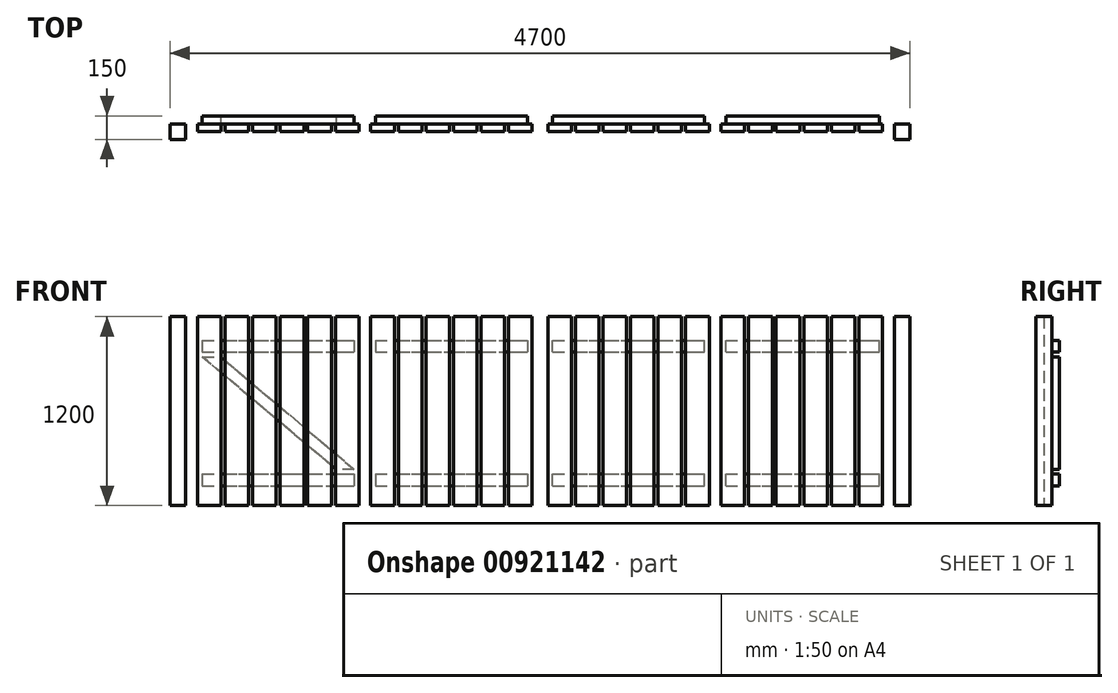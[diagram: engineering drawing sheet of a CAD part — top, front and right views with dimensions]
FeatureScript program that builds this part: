
annotation { "Feature Type Name" : "Feature", "Feature Type Description" : "" }
export const myFeature = defineFeature(function(context is Context, id is Id, definition is map)
    precondition{}
    {
        {
            var Q0;
            Q0=qCreatedBy(makeId("Front.planeOp"),FACE);
            var sketch = newSketch(context, id + "F0", { "sketchPlane" : qUnion([Q0])});
            skLineSegment(sketch, "E0.bottom", {"start": v(-2350, 1200) * mm, "end": v(-2250, 1200) * mm});
            skLineSegment(sketch, "E0.top", {"start": v(-2350, 0) * mm, "end": v(-2250, 0) * mm});
            skLineSegment(sketch, "E0.left", {"start": v(-2350, 1200) * mm, "end": v(-2350, 0) * mm});
            skLineSegment(sketch, "E0.right", {"start": v(-2250, 1200) * mm, "end": v(-2250, 0) * mm});
            skLineSegment(sketch, "E1.bottom", {"start": v(2250, 0) * mm, "end": v(2350, 0) * mm});
            skLineSegment(sketch, "E1.top", {"start": v(2250, 1200) * mm, "end": v(2350, 1200) * mm});
            skLineSegment(sketch, "E1.left", {"start": v(2250, 0) * mm, "end": v(2250, 1200) * mm});
            skLineSegment(sketch, "E1.right", {"start": v(2350, 0) * mm, "end": v(2350, 1200) * mm});
            skSolve(sketch);
        }
        {
            var Q0;
            Q0=makeQuery(id+"F0.imprint","IMPRINT",FACE,{"disambiguationData":[TD([[makeQuery(id+"F0.imprint","IMPRINT",EDGE,{"derivedFrom":sQuery(id+"F0.wireOp",EDGE,"E0.bottom")}),-1.0]])]});
            var Q1;
            Q1=makeQuery(id+"F0.imprint","IMPRINT",FACE,{"disambiguationData":[TD([[makeQuery(id+"F0.imprint","IMPRINT",EDGE,{"derivedFrom":sQuery(id+"F0.wireOp",EDGE,"E1.bottom")}),1.0]])]});
            extrude(context, id + "F1", {"entities" : qUnion([Q0, Q1]), "depth" : 100 * mm, "offsetDistance" : 25.4 * mm});
        }
        {
            var Q0;
            Q0=qCreatedBy(makeId("Front.planeOp"),FACE);
            var sketch = newSketch(context, id + "F2", { "sketchPlane" : qUnion([Q0])});
            skLineSegment(sketch, "E2.bottom", {"start": v(-2175, 1200) * mm, "end": v(-2025, 1200) * mm});
            skLineSegment(sketch, "E2.top", {"start": v(-2175, 0) * mm, "end": v(-2025, 0) * mm});
            skLineSegment(sketch, "E2.left", {"start": v(-2175, 1200) * mm, "end": v(-2175, 0) * mm});
            skLineSegment(sketch, "E2.right", {"start": v(-2025, 1200) * mm, "end": v(-2025, 0) * mm});
            skLineSegment(sketch, "E3.bottom", {"start": v(-50, 0) * mm, "end": v(-200, 0) * mm});
            skLineSegment(sketch, "E3.top", {"start": v(-50, 1200) * mm, "end": v(-200, 1200) * mm});
            skLineSegment(sketch, "E3.left", {"start": v(-50, 0) * mm, "end": v(-50, 1200) * mm});
            skLineSegment(sketch, "E3.right", {"start": v(-200, 0) * mm, "end": v(-200, 1200) * mm});
            skLineSegment(sketch, "E4.bottom", {"start": v(50, 0) * mm, "end": v(200, 0) * mm});
            skLineSegment(sketch, "E4.top", {"start": v(50, 1200) * mm, "end": v(200, 1200) * mm});
            skLineSegment(sketch, "E4.left", {"start": v(50, 0) * mm, "end": v(50, 1200) * mm});
            skLineSegment(sketch, "E4.right", {"start": v(200, 0) * mm, "end": v(200, 1200) * mm});
            skLineSegment(sketch, "E5.bottom", {"start": v(2175, 0) * mm, "end": v(2025, 0) * mm});
            skLineSegment(sketch, "E5.top", {"start": v(2175, 1200) * mm, "end": v(2025, 1200) * mm});
            skLineSegment(sketch, "E5.left", {"start": v(2175, 0) * mm, "end": v(2175, 1200) * mm});
            skLineSegment(sketch, "E5.right", {"start": v(2025, 0) * mm, "end": v(2025, 1200) * mm});
            skLineSegment(sketch, "E6.1.0.0", {"start": v(-2000, 1200) * mm, "end": v(-1850, 1200) * mm});
            skLineSegment(sketch, "E6.1.0.1", {"start": v(-2000, 1200) * mm, "end": v(-2000, 0) * mm});
            skLineSegment(sketch, "E6.1.0.2", {"start": v(-2000, 0) * mm, "end": v(-1850, 0) * mm});
            skLineSegment(sketch, "E6.1.0.3", {"start": v(-1850, 1200) * mm, "end": v(-1850, 0) * mm});
            skLineSegment(sketch, "E6.2.0.0", {"start": v(-1825, 1200) * mm, "end": v(-1675, 1200) * mm});
            skLineSegment(sketch, "E6.2.0.1", {"start": v(-1825, 1200) * mm, "end": v(-1825, 0) * mm});
            skLineSegment(sketch, "E6.2.0.2", {"start": v(-1825, 0) * mm, "end": v(-1675, 0) * mm});
            skLineSegment(sketch, "E6.2.0.3", {"start": v(-1675, 1200) * mm, "end": v(-1675, 0) * mm});
            skLineSegment(sketch, "E6.3.0.0", {"start": v(-1650, 1200) * mm, "end": v(-1500, 1200) * mm});
            skLineSegment(sketch, "E6.3.0.1", {"start": v(-1650, 1200) * mm, "end": v(-1650, 0) * mm});
            skLineSegment(sketch, "E6.3.0.2", {"start": v(-1650, 0) * mm, "end": v(-1500, 0) * mm});
            skLineSegment(sketch, "E6.3.0.3", {"start": v(-1500, 1200) * mm, "end": v(-1500, 0) * mm});
            skLineSegment(sketch, "E6.4.0.0", {"start": v(-1475, 1200) * mm, "end": v(-1325, 1200) * mm});
            skLineSegment(sketch, "E6.4.0.1", {"start": v(-1475, 1200) * mm, "end": v(-1475, 0) * mm});
            skLineSegment(sketch, "E6.4.0.2", {"start": v(-1475, 0) * mm, "end": v(-1325, 0) * mm});
            skLineSegment(sketch, "E6.4.0.3", {"start": v(-1325, 1200) * mm, "end": v(-1325, 0) * mm});
            skLineSegment(sketch, "E6.5.0.0", {"start": v(-1300, 1200) * mm, "end": v(-1150, 1200) * mm});
            skLineSegment(sketch, "E6.5.0.1", {"start": v(-1300, 1200) * mm, "end": v(-1300, 0) * mm});
            skLineSegment(sketch, "E6.5.0.2", {"start": v(-1300, 0) * mm, "end": v(-1150, 0) * mm});
            skLineSegment(sketch, "E6.5.0.3", {"start": v(-1150, 1200) * mm, "end": v(-1150, 0) * mm});
            skLineSegment(sketch, "E6.direction1", {"start": v(-2175, 0) * mm, "end": v(-2000, 0) * mm, "construction": true});
            skLineSegment(sketch, "E7.1.0.0", {"start": v(-375, 0) * mm, "end": v(-375, 1200) * mm});
            skLineSegment(sketch, "E7.1.0.1", {"start": v(-225, 1200) * mm, "end": v(-375, 1200) * mm});
            skLineSegment(sketch, "E7.1.0.2", {"start": v(-225, 0) * mm, "end": v(-225, 1200) * mm});
            skLineSegment(sketch, "E7.1.0.3", {"start": v(-225, 0) * mm, "end": v(-375, 0) * mm});
            skLineSegment(sketch, "E7.2.0.0", {"start": v(-550, 0) * mm, "end": v(-550, 1200) * mm});
            skLineSegment(sketch, "E7.2.0.1", {"start": v(-400, 1200) * mm, "end": v(-550, 1200) * mm});
            skLineSegment(sketch, "E7.2.0.2", {"start": v(-400, 0) * mm, "end": v(-400, 1200) * mm});
            skLineSegment(sketch, "E7.2.0.3", {"start": v(-400, 0) * mm, "end": v(-550, 0) * mm});
            skLineSegment(sketch, "E7.3.0.0", {"start": v(-725, 0) * mm, "end": v(-725, 1200) * mm});
            skLineSegment(sketch, "E7.3.0.1", {"start": v(-575, 1200) * mm, "end": v(-725, 1200) * mm});
            skLineSegment(sketch, "E7.3.0.2", {"start": v(-575, 0) * mm, "end": v(-575, 1200) * mm});
            skLineSegment(sketch, "E7.3.0.3", {"start": v(-575, 0) * mm, "end": v(-725, 0) * mm});
            skLineSegment(sketch, "E7.4.0.0", {"start": v(-900, 0) * mm, "end": v(-900, 1200) * mm});
            skLineSegment(sketch, "E7.4.0.1", {"start": v(-750, 1200) * mm, "end": v(-900, 1200) * mm});
            skLineSegment(sketch, "E7.4.0.2", {"start": v(-750, 0) * mm, "end": v(-750, 1200) * mm});
            skLineSegment(sketch, "E7.4.0.3", {"start": v(-750, 0) * mm, "end": v(-900, 0) * mm});
            skLineSegment(sketch, "E7.5.0.0", {"start": v(-1075, 0) * mm, "end": v(-1075, 1200) * mm});
            skLineSegment(sketch, "E7.5.0.1", {"start": v(-925, 1200) * mm, "end": v(-1075, 1200) * mm});
            skLineSegment(sketch, "E7.5.0.2", {"start": v(-925, 0) * mm, "end": v(-925, 1200) * mm});
            skLineSegment(sketch, "E7.5.0.3", {"start": v(-925, 0) * mm, "end": v(-1075, 0) * mm});
            skLineSegment(sketch, "E7.direction1", {"start": v(-200, 0) * mm, "end": v(-375, 0) * mm, "construction": true});
            skLineSegment(sketch, "E8.1.0.0", {"start": v(375, 0) * mm, "end": v(375, 1200) * mm});
            skLineSegment(sketch, "E8.1.0.1", {"start": v(225, 1200) * mm, "end": v(375, 1200) * mm});
            skLineSegment(sketch, "E8.1.0.2", {"start": v(225, 0) * mm, "end": v(225, 1200) * mm});
            skLineSegment(sketch, "E8.1.0.3", {"start": v(225, 0) * mm, "end": v(375, 0) * mm});
            skLineSegment(sketch, "E8.2.0.0", {"start": v(550, 0) * mm, "end": v(550, 1200) * mm});
            skLineSegment(sketch, "E8.2.0.1", {"start": v(400, 1200) * mm, "end": v(550, 1200) * mm});
            skLineSegment(sketch, "E8.2.0.2", {"start": v(400, 0) * mm, "end": v(400, 1200) * mm});
            skLineSegment(sketch, "E8.2.0.3", {"start": v(400, 0) * mm, "end": v(550, 0) * mm});
            skLineSegment(sketch, "E8.3.0.0", {"start": v(725, 0) * mm, "end": v(725, 1200) * mm});
            skLineSegment(sketch, "E8.3.0.1", {"start": v(575, 1200) * mm, "end": v(725, 1200) * mm});
            skLineSegment(sketch, "E8.3.0.2", {"start": v(575, 0) * mm, "end": v(575, 1200) * mm});
            skLineSegment(sketch, "E8.3.0.3", {"start": v(575, 0) * mm, "end": v(725, 0) * mm});
            skLineSegment(sketch, "E8.4.0.0", {"start": v(900, 0) * mm, "end": v(900, 1200) * mm});
            skLineSegment(sketch, "E8.4.0.1", {"start": v(750, 1200) * mm, "end": v(900, 1200) * mm});
            skLineSegment(sketch, "E8.4.0.2", {"start": v(750, 0) * mm, "end": v(750, 1200) * mm});
            skLineSegment(sketch, "E8.4.0.3", {"start": v(750, 0) * mm, "end": v(900, 0) * mm});
            skLineSegment(sketch, "E8.5.0.0", {"start": v(1075, 0) * mm, "end": v(1075, 1200) * mm});
            skLineSegment(sketch, "E8.5.0.1", {"start": v(925, 1200) * mm, "end": v(1075, 1200) * mm});
            skLineSegment(sketch, "E8.5.0.2", {"start": v(925, 0) * mm, "end": v(925, 1200) * mm});
            skLineSegment(sketch, "E8.5.0.3", {"start": v(925, 0) * mm, "end": v(1075, 0) * mm});
            skLineSegment(sketch, "E8.direction1", {"start": v(50, 0) * mm, "end": v(225, 0) * mm, "construction": true});
            skLineSegment(sketch, "E9.1.0.0", {"start": v(1850, 0) * mm, "end": v(1850, 1200) * mm});
            skLineSegment(sketch, "E9.1.0.1", {"start": v(2000, 0) * mm, "end": v(1850, 0) * mm});
            skLineSegment(sketch, "E9.1.0.2", {"start": v(2000, 0) * mm, "end": v(2000, 1200) * mm});
            skLineSegment(sketch, "E9.1.0.3", {"start": v(2000, 1200) * mm, "end": v(1850, 1200) * mm});
            skLineSegment(sketch, "E9.2.0.0", {"start": v(1675, 0) * mm, "end": v(1675, 1200) * mm});
            skLineSegment(sketch, "E9.2.0.1", {"start": v(1825, 0) * mm, "end": v(1675, 0) * mm});
            skLineSegment(sketch, "E9.2.0.2", {"start": v(1825, 0) * mm, "end": v(1825, 1200) * mm});
            skLineSegment(sketch, "E9.2.0.3", {"start": v(1825, 1200) * mm, "end": v(1675, 1200) * mm});
            skLineSegment(sketch, "E9.3.0.0", {"start": v(1500, 0) * mm, "end": v(1500, 1200) * mm});
            skLineSegment(sketch, "E9.3.0.1", {"start": v(1650, 0) * mm, "end": v(1500, 0) * mm});
            skLineSegment(sketch, "E9.3.0.2", {"start": v(1650, 0) * mm, "end": v(1650, 1200) * mm});
            skLineSegment(sketch, "E9.3.0.3", {"start": v(1650, 1200) * mm, "end": v(1500, 1200) * mm});
            skLineSegment(sketch, "E9.4.0.0", {"start": v(1325, 0) * mm, "end": v(1325, 1200) * mm});
            skLineSegment(sketch, "E9.4.0.1", {"start": v(1475, 0) * mm, "end": v(1325, 0) * mm});
            skLineSegment(sketch, "E9.4.0.2", {"start": v(1475, 0) * mm, "end": v(1475, 1200) * mm});
            skLineSegment(sketch, "E9.4.0.3", {"start": v(1475, 1200) * mm, "end": v(1325, 1200) * mm});
            skLineSegment(sketch, "E9.5.0.0", {"start": v(1150, 0) * mm, "end": v(1150, 1200) * mm});
            skLineSegment(sketch, "E9.5.0.1", {"start": v(1300, 0) * mm, "end": v(1150, 0) * mm});
            skLineSegment(sketch, "E9.5.0.2", {"start": v(1300, 0) * mm, "end": v(1300, 1200) * mm});
            skLineSegment(sketch, "E9.5.0.3", {"start": v(1300, 1200) * mm, "end": v(1150, 1200) * mm});
            skLineSegment(sketch, "E9.direction1", {"start": v(2025, 0) * mm, "end": v(1850, 0) * mm, "construction": true});
            skSolve(sketch);
        }
        {
            var Q0;
            Q0 = qSketchRegion(id + "F2", true);
            extrude(context, id + "F3", {"entities" : qUnion([Q0]), "depth" : 50 * mm, "offsetDistance" : 25.4 * mm});
        }
        {
            var Q0;
            Q0=qCreatedBy(makeId("Front.planeOp"),FACE);
            var sketch = newSketch(context, id + "F4", { "sketchPlane" : qUnion([Q0])});
            skLineSegment(sketch, "E10.bottom", {"start": v(-2145, 1050) * mm, "end": v(-1180, 1050) * mm});
            skLineSegment(sketch, "E10.top", {"start": v(-2145, 975) * mm, "end": v(-1180, 975) * mm});
            skLineSegment(sketch, "E10.left", {"start": v(-2145, 1050) * mm, "end": v(-2145, 975) * mm});
            skLineSegment(sketch, "E10.right", {"start": v(-1180, 1050) * mm, "end": v(-1180, 975) * mm});
            skLineSegment(sketch, "E11.bottom", {"start": v(-1045, 1050) * mm, "end": v(-80, 1050) * mm});
            skLineSegment(sketch, "E11.top", {"start": v(-1045, 975) * mm, "end": v(-80, 975) * mm});
            skLineSegment(sketch, "E11.left", {"start": v(-1045, 1050) * mm, "end": v(-1045, 975) * mm});
            skLineSegment(sketch, "E11.right", {"start": v(-80, 1050) * mm, "end": v(-80, 975) * mm});
            skPoint(sketch, "E12.oppositeSnap0", {"position": v(-562.5, 1050) * mm});
            skLineSegment(sketch, "E12.bottom", {"start": v(80, 975) * mm, "end": v(1045, 975) * mm});
            skLineSegment(sketch, "E12.top", {"start": v(80, 1050) * mm, "end": v(1045, 1050) * mm});
            skLineSegment(sketch, "E12.left", {"start": v(80, 975) * mm, "end": v(80, 1050) * mm});
            skLineSegment(sketch, "E12.right", {"start": v(1045, 975) * mm, "end": v(1045, 1050) * mm});
            skLineSegment(sketch, "E13.bottom", {"start": v(1180, 975) * mm, "end": v(2155, 975) * mm});
            skLineSegment(sketch, "E13.top", {"start": v(1180, 1050) * mm, "end": v(2155, 1050) * mm});
            skLineSegment(sketch, "E13.left", {"start": v(1180, 975) * mm, "end": v(1180, 1050) * mm});
            skLineSegment(sketch, "E13.right", {"start": v(2155, 975) * mm, "end": v(2155, 1050) * mm});
            skLineSegment(sketch, "E14.0.1.0", {"start": v(1180, 125) * mm, "end": v(2155, 125) * mm});
            skLineSegment(sketch, "E14.0.1.1", {"start": v(-2145, 200) * mm, "end": v(-1180, 200) * mm});
            skLineSegment(sketch, "E14.0.1.2", {"start": v(1180, 200) * mm, "end": v(2155, 200) * mm});
            skLineSegment(sketch, "E14.0.1.3", {"start": v(-1045, 200) * mm, "end": v(-80, 200) * mm});
            skLineSegment(sketch, "E14.0.1.4", {"start": v(-1045, 125) * mm, "end": v(-80, 125) * mm});
            skPoint(sketch, "E14.0.1.5", {"position": v(-562.5, 200) * mm});
            skLineSegment(sketch, "E14.0.1.6", {"start": v(80, 125) * mm, "end": v(1045, 125) * mm});
            skLineSegment(sketch, "E14.0.1.7", {"start": v(80, 200) * mm, "end": v(1045, 200) * mm});
            skLineSegment(sketch, "E14.0.1.8", {"start": v(-2145, 125) * mm, "end": v(-1180, 125) * mm});
            skLineSegment(sketch, "E14.0.1.9", {"start": v(80, 125) * mm, "end": v(80, 200) * mm});
            skLineSegment(sketch, "E14.0.1.10", {"start": v(1180, 125) * mm, "end": v(1180, 200) * mm});
            skLineSegment(sketch, "E14.0.1.11", {"start": v(2155, 125) * mm, "end": v(2155, 200) * mm});
            skLineSegment(sketch, "E14.0.1.12", {"start": v(-1180, 200) * mm, "end": v(-1180, 125) * mm});
            skLineSegment(sketch, "E14.0.1.13", {"start": v(1045, 125) * mm, "end": v(1045, 200) * mm});
            skLineSegment(sketch, "E14.0.1.14", {"start": v(-1045, 200) * mm, "end": v(-1045, 125) * mm});
            skLineSegment(sketch, "E14.0.1.15", {"start": v(-2145, 200) * mm, "end": v(-2145, 125) * mm});
            skLineSegment(sketch, "E14.0.1.16", {"start": v(-80, 200) * mm, "end": v(-80, 125) * mm});
            skLineSegment(sketch, "E14.direction1", {"start": v(-2145, 975) * mm, "end": v(-2119.6, 975) * mm, "construction": true});
            skLineSegment(sketch, "E14.direction2", {"start": v(-2145, 975) * mm, "end": v(-2145, 125) * mm, "construction": true});
            skLineSegment(sketch, "E15", {"start": v(-1180, 230) * mm, "end": v(-1296.4, 230) * mm});
            skLineSegment(sketch, "E16", {"start": v(-1296.4, 230) * mm, "end": v(-2145, 945) * mm});
            skLineSegment(sketch, "E17", {"start": v(-2145, 945) * mm, "end": v(-2028.6, 945) * mm});
            skLineSegment(sketch, "E18", {"start": v(-2028.6, 945) * mm, "end": v(-1180, 230) * mm});
            skSolve(sketch);
        }
        {
            var Q0;
            Q0 = qSketchRegion(id + "F4", true);
            extrude(context, id + "F5", {"entities" : qUnion([Q0]), "oppositeDirection" : true, "depth" : 50 * mm, "offsetDistance" : 25.4 * mm});
        }
    });
